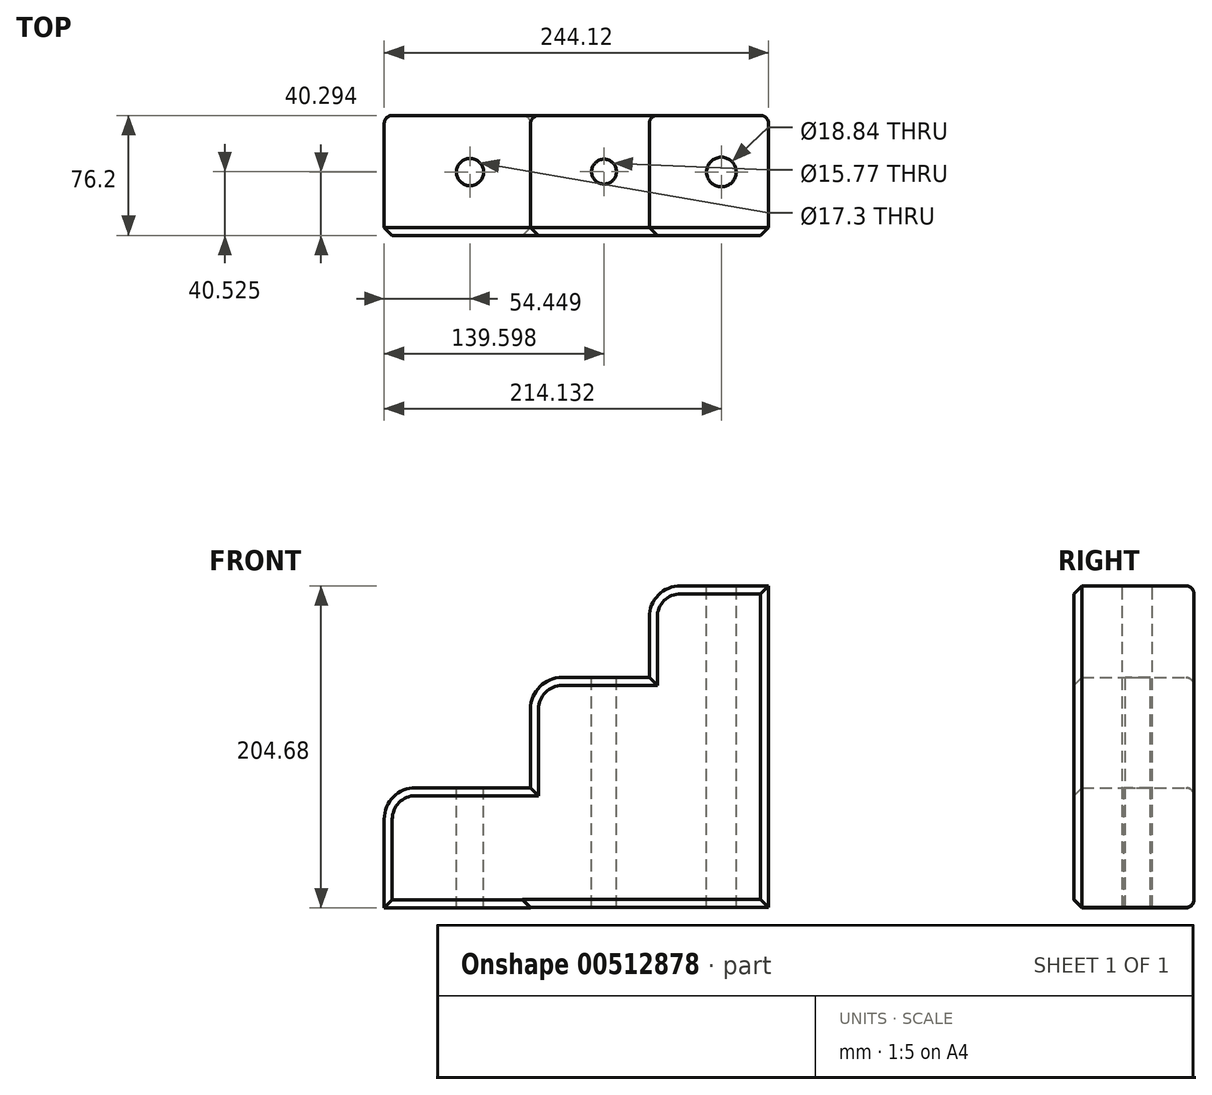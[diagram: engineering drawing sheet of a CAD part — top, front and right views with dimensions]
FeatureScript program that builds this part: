
annotation { "Feature Type Name" : "Feature", "Feature Type Description" : "" }
export const myFeature = defineFeature(function(context is Context, id is Id, definition is map)
    precondition{}
    {
        {
            var Q0;
            Q0=qCreatedBy(makeId("Front.planeOp"),FACE);
            var sketch = newSketch(context, id + "F0", { "sketchPlane" : qUnion([Q0])});
            skLineSegment(sketch, "E0.bottom", {"start": v(-75.36, -76.06) * mm, "end": v(75.82, -76.06) * mm});
            skLineSegment(sketch, "E0.top", {"start": v(-75.36, -34.2) * mm, "end": v(75.82, -34.2) * mm});
            skLineSegment(sketch, "E0.left", {"start": v(-75.36, -76.06) * mm, "end": v(-75.36, -34.2) * mm});
            skLineSegment(sketch, "E0.right", {"start": v(75.82, -76.06) * mm, "end": v(75.82, -34.2) * mm});
            skLineSegment(sketch, "E1.bottom", {"start": v(0, -34.2) * mm, "end": v(75.82, -34.2) * mm});
            skLineSegment(sketch, "E1.top", {"start": v(0, 0) * mm, "end": v(75.82, 0) * mm});
            skLineSegment(sketch, "E1.left", {"start": v(0, -34.2) * mm, "end": v(0, 0) * mm});
            skLineSegment(sketch, "E1.right", {"start": v(75.82, -34.2) * mm, "end": v(75.82, 0) * mm});
            skLineSegment(sketch, "E2.bottom", {"start": v(75.82, 0) * mm, "end": v(0, 0) * mm});
            skLineSegment(sketch, "E2.top", {"start": v(75.82, 70) * mm, "end": v(0, 70) * mm});
            skLineSegment(sketch, "E2.left", {"start": v(75.82, 0) * mm, "end": v(75.82, 70) * mm});
            skLineSegment(sketch, "E2.right", {"start": v(0, 0) * mm, "end": v(0, 70) * mm});
            skLineSegment(sketch, "E3.bottom", {"start": v(0, 0) * mm, "end": v(-75.36, 0) * mm});
            skLineSegment(sketch, "E3.top", {"start": v(0, -34.2) * mm, "end": v(-75.36, -34.2) * mm});
            skLineSegment(sketch, "E3.left", {"start": v(0, 0) * mm, "end": v(0, -34.2) * mm});
            skLineSegment(sketch, "E3.right", {"start": v(-75.36, 0) * mm, "end": v(-75.36, -34.2) * mm});
            skLineSegment(sketch, "E4.bottom", {"start": v(-75.36, 0) * mm, "end": v(-168.3, 0) * mm});
            skLineSegment(sketch, "E4.top", {"start": v(-75.36, -76.43) * mm, "end": v(-168.3, -76.43) * mm});
            skLineSegment(sketch, "E4.left", {"start": v(-75.36, 0) * mm, "end": v(-75.36, -76.43) * mm});
            skLineSegment(sketch, "E4.right", {"start": v(-168.3, 0) * mm, "end": v(-168.3, -76.43) * mm});
            skLineSegment(sketch, "E5.bottom", {"start": v(-75.36, 0) * mm, "end": v(0, 0) * mm});
            skLineSegment(sketch, "E5.top", {"start": v(-75.36, 70) * mm, "end": v(0, 70) * mm});
            skLineSegment(sketch, "E5.left", {"start": v(-75.36, 0) * mm, "end": v(-75.36, 70) * mm});
            skLineSegment(sketch, "E6.top", {"start": v(75.82, 128.25) * mm, "end": v(0, 128.25) * mm});
            skLineSegment(sketch, "E6.left", {"start": v(75.82, 70) * mm, "end": v(75.82, 128.25) * mm});
            skLineSegment(sketch, "E6.right", {"start": v(0, 70) * mm, "end": v(0, 128.25) * mm});
            skSolve(sketch);
        }
        {
            var Q0;
            Q0 = qSketchRegion(id + "F0", true);
            extrude(context, id + "F1", {"entities" : qUnion([Q0]), "depth" : 76.2 * mm});
        }
        {
            var Q0;
            Q0 = qSketchRegion(id + "F0", true);
            extrude(context, id + "F2", {"entities" : qUnion([Q0]), "operationType" : NewBodyOperationType.ADD, "depth" : 30 * mm});
        }
        {
            var Q0;
            Q0=makeQuery(id+"F1.opExtrude","SWEPT_EDGE",EDGE,{"disambiguationData":[OSD([sQuery(id+"F0.wireOp",EDGE,"E6.top"),sQuery(id+"F0.wireOp",EDGE,"E6.right")])]});
            var Q1;
            Q1=makeQuery(id+"F1.opExtrude","SWEPT_EDGE",EDGE,{"disambiguationData":[OSD([sQuery(id+"F0.wireOp",EDGE,"E5.top"),sQuery(id+"F0.wireOp",EDGE,"E5.left")])]});
            var Q2;
            Q2=makeQuery(id+"F1.opExtrude","SWEPT_EDGE",EDGE,{"disambiguationData":[OSD([sQuery(id+"F0.wireOp",EDGE,"E4.bottom"),sQuery(id+"F0.wireOp",EDGE,"E4.right")])]});
            fillet(context, id + "F3", {"entities" : qUnion([Q0, Q1, Q2]), "radius" : 20 * mm, "tangentPropagation" : true, "allowEdgeOverflow" : false});
        }
        {
            var Q0;
            Q0=makeQuery(id+"F1.opExtrude","CAP_FACE",FACE,{"disambiguationData":[OSD([sQuery(id+"F0.wireOp",EDGE,"E0.bottom"),sQuery(id+"F0.wireOp",EDGE,"E0.right"),sQuery(id+"F0.wireOp",EDGE,"E1.right"),sQuery(id+"F0.wireOp",EDGE,"E2.left"),sQuery(id+"F0.wireOp",EDGE,"E4.bottom"),sQuery(id+"F0.wireOp",EDGE,"E4.top"),sQuery(id+"F0.wireOp",EDGE,"E4.left"),sQuery(id+"F0.wireOp",EDGE,"E4.right"),sQuery(id+"F0.wireOp",EDGE,"E5.top"),sQuery(id+"F0.wireOp",EDGE,"E5.left"),sQuery(id+"F0.wireOp",EDGE,"E6.top"),sQuery(id+"F0.wireOp",EDGE,"E6.left"),sQuery(id+"F0.wireOp",EDGE,"E6.right"),sQuery(id+"F0.wireOp",EDGE,"kpRBIJfL-Pq4D-xn1N-BZhB-C1bFulMz3jPF")])],"isStart":false});
            chamfer(context, id + "F4", {"entities" : qUnion([Q0]), "width" : 5.08 * mm, "tangentPropagation" : true});
        }
        {
            var Q0;
            Q0=makeQuery(id+"F1.opExtrude","CAP_FACE",FACE,{"disambiguationData":[OSD([sQuery(id+"F0.wireOp",EDGE,"E0.bottom"),sQuery(id+"F0.wireOp",EDGE,"E0.right"),sQuery(id+"F0.wireOp",EDGE,"E1.right"),sQuery(id+"F0.wireOp",EDGE,"E2.left"),sQuery(id+"F0.wireOp",EDGE,"E4.bottom"),sQuery(id+"F0.wireOp",EDGE,"E4.top"),sQuery(id+"F0.wireOp",EDGE,"E4.left"),sQuery(id+"F0.wireOp",EDGE,"E4.right"),sQuery(id+"F0.wireOp",EDGE,"E5.top"),sQuery(id+"F0.wireOp",EDGE,"E5.left"),sQuery(id+"F0.wireOp",EDGE,"E6.top"),sQuery(id+"F0.wireOp",EDGE,"E6.left"),sQuery(id+"F0.wireOp",EDGE,"E6.right"),sQuery(id+"F0.wireOp",EDGE,"kpRBIJfL-Pq4D-xn1N-BZhB-C1bFulMz3jPF")])],"isStart":true});
            fillet(context, id + "F5", {"entities" : qUnion([Q0]), "radius" : 5.08 * mm, "tangentPropagation" : true, "allowEdgeOverflow" : false});
        }
        {
            var Q0;
            Q0=makeQuery(id+"F1.opExtrude","SWEPT_FACE",FACE,{"disambiguationData":[OSD([sQuery(id+"F0.wireOp",EDGE,"E6.top")])]});
            var sketch = newSketch(context, id + "F6", { "sketchPlane" : qUnion([Q0])});
            skCircle(sketch, "E7", {"center": v(-113.85, -35.9) * mm, "radius": 8.65 * mm});
            skCircle(sketch, "E8", {"center": v(-28.7, -35.67) * mm, "radius": 7.89 * mm});
            skCircle(sketch, "E9", {"center": v(45.83, -35.9) * mm, "radius": 9.42 * mm});
            skSolve(sketch);
        }
        {
            var Q0;
            Q0 = qSketchRegion(id + "F6", true);
            extrude(context, id + "F7", {"entities" : qUnion([Q0]), "operationType" : NewBodyOperationType.REMOVE, "endBound" : BoundingType.THROUGH_ALL, "oppositeDirection" : true, "depth" : 25 * mm, "offsetDistance" : 25 * mm});
        }
    });
